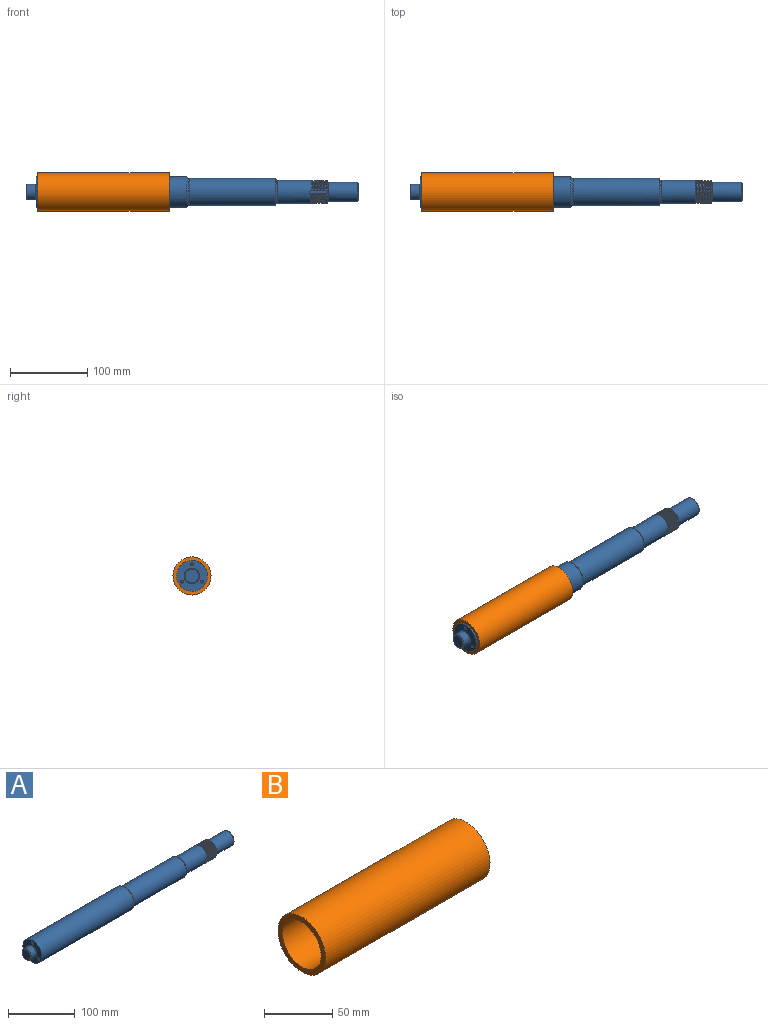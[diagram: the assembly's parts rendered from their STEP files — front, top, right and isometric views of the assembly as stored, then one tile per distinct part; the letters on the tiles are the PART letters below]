
ASSEMBLY  parts=2 mates=1
PART A: 82 faces, bbox 429x40x40 mm
  f0: cylinder r=15mm len=30mm, axis (-1,0,0), area 22.3mm2, adj f11,f28,f61,f63
  f1: cylinder r=15mm len=30mm, axis (-1,0,0), area 22.3mm2, adj f12,f29,f61,f63
  f2: cylinder r=15mm len=30mm, axis (-1,0,0), area 22.3mm2, adj f13,f30,f61,f63
  f3: cylinder r=15mm len=30mm, axis (-1,0,0), area 22.3mm2, adj f14,f31,f61,f63
  f4: cylinder r=15mm len=30mm, axis (-1,0,0), area 22.3mm2, adj f15,f32,f61,f63
  f5: cylinder r=15mm len=30mm, axis (-1,0,0), area 22.3mm2, adj f16,f33,f61,f63
  f6: cylinder r=15mm len=30mm, axis (-1,0,0), area 22.3mm2, adj f17,f34,f61,f63
  f7: cylinder r=15mm len=30mm, axis (-1,0,0), area 22.3mm2, adj f18,f35,f61,f63
  f8: cylinder r=15mm len=30mm, axis (-1,0,0), area 22.3mm2, adj f36,f55,f61,f63
  f9: cylinder r=15mm len=30mm, axis (-1,0,0), area 89.2mm2, adj f10,f48,f61,f63
  f10: bspline ~31.54x30mm, area 107.3mm2, adj f9,f19,f61,f63
  f11: bspline ~31.54x30mm, area 107.3mm2, adj f0,f20,f61,f63
  f12: bspline ~31.54x30mm, area 107.3mm2, adj f1,f21,f61,f63
  f13: bspline ~31.54x30mm, area 107.3mm2, adj f2,f22,f61,f63
  f14: bspline ~31.54x30mm, area 107.3mm2, adj f3,f23,f61,f63
  f15: bspline ~31.54x30mm, area 107.3mm2, adj f4,f24,f61,f63
  f16: bspline ~31.54x30mm, area 107.3mm2, adj f5,f25,f61,f63
  f17: bspline ~31.54x30mm, area 107.3mm2, adj f6,f26,f61,f63
  f18: bspline ~31.54x30mm, area 107.3mm2, adj f7,f27,f61,f63
  f19: cylinder r=13.92mm len=27.84mm, axis (1,0,0), area 41.2mm2, adj f10,f28,f61,f63
  f20: cylinder r=13.92mm len=27.84mm, axis (1,0,0), area 41.2mm2, adj f11,f29,f61,f63
  f21: cylinder r=13.92mm len=27.84mm, axis (1,0,0), area 41.2mm2, adj f12,f30,f61,f63
  f22: cylinder r=13.92mm len=27.84mm, axis (1,0,0), area 41.2mm2, adj f13,f31,f61,f63
  f23: cylinder r=13.92mm len=27.84mm, axis (1,0,0), area 41.2mm2, adj f14,f32,f61,f63
  f24: cylinder r=13.92mm len=27.84mm, axis (1,0,0), area 41.2mm2, adj f15,f33,f61,f63
  f25: cylinder r=13.92mm len=27.84mm, axis (1,0,0), area 41.2mm2, adj f16,f34,f61,f63
  f26: cylinder r=13.92mm len=27.84mm, axis (1,0,0), area 41.2mm2, adj f17,f35,f61,f63
  f27: cylinder r=13.92mm len=27.84mm, axis (1,0,0), area 41.2mm2, adj f18,f36,f61,f63
  f28: bspline ~31.54x30mm, area 107.3mm2, adj f0,f19,f61,f63
  f29: bspline ~31.54x30mm, area 107.3mm2, adj f1,f20,f61,f63
  f30: bspline ~31.54x30mm, area 107.3mm2, adj f2,f21,f61,f63
  f31: bspline ~31.54x30mm, area 107.3mm2, adj f3,f22,f61,f63
  f32: bspline ~31.54x30mm, area 107.3mm2, adj f4,f23,f61,f63
  f33: bspline ~31.54x30mm, area 107.3mm2, adj f5,f24,f61,f63
  f34: bspline ~31.54x30mm, area 107.3mm2, adj f6,f25,f61,f63
  f35: bspline ~31.54x30mm, area 107.3mm2, adj f7,f26,f61,f63
  f36: bspline ~31.54x30mm, area 107.3mm2, adj f8,f27,f61,f63
  f37: cylinder r=17.5mm len=111mm, axis (-1,0,0), area 12205.1mm2, adj f39,f40
  f38: plane 31x31mm, normal (1,0,0), area 94.2mm2, adj f39,f46
  f39: cone r=17.5mm half-angle=45deg, axis (-1,0,0), area 293.2mm2, adj f37,f38
  f40: plane 35x35mm, normal (-1,0,0), area 54.2mm2, adj f37,f41
  f41: cylinder r=17mm len=34mm, axis (-1,0,0), area 106.8mm2, adj f40,f44
  f42: cylinder r=20mm len=195mm, axis (-1,0,0), area 24504.4mm2, adj f43,f77
  f43: cone r=20mm half-angle=45deg, axis (-1,0,0), area 337.7mm2, adj f42,f44
  f44: plane 36x36mm, normal (1,0,0), area 110mm2, adj f41,f43
  f45: plane 30x30mm, normal (-1,0,0), area 46.3mm2, adj f46,f49
  f46: cylinder r=14.5mm len=29mm, axis (-1,0,0), area 91.1mm2, adj f38,f45
  f47: plane 28x27.81mm, normal (1,0,0), area 156.8mm2, adj f48,f51,f58,f59,f60
  f48: cone r=15mm half-angle=45deg, axis (-1,0,0), area 121.9mm2, adj f9,f47,f58,f59
  f49: cylinder r=15mm len=44.2mm, axis (-1,0,0), area 4069.8mm2, adj f45,f57,f62,f63
  f50: plane 25x25mm, normal (-1,0,0), area 38.5mm2, adj f51,f54
  f51: cylinder r=12mm len=24mm, axis (-1,0,0), area 75.4mm2, adj f47,f50
  f52: plane 23x23mm, normal (1,0,0), area 364.6mm2, adj f53,f65
  f53: cone r=12.5mm half-angle=45deg, axis (-1,0,0), area 106.6mm2, adj f52,f54
  f54: cylinder r=12.5mm len=37mm, axis (-1,0,0), area 2906mm2, adj f50,f53
  f55: bspline ~31.54x30mm, area 107.3mm2, adj f8,f56,f61,f62,f63
  f56: cylinder r=13.92mm len=27.84mm, axis (1,0,0), area 41.3mm2, adj f55,f57,f62,f63
  f57: bspline ~31.54x30mm, area 107.9mm2, adj f49,f56,f62,f63
  f58: cylinder r=2.5mm len=2.29mm, axis (0,-1,0), area 1.9mm2, adj f47,f48,f60,f63
  f59: cylinder r=2.5mm len=2.29mm, axis (0,-1,0), area 1.9mm2, adj f47,f48,f60,f61
  f60: plane 23.5x5mm, normal (0,-1,0), area 114.7mm2, adj f47,f58,f59,f61,f62,f63
  f61: plane 20.01x2.3mm, normal (0,0,1), area 34.7mm2, adj f0,f1,f2,f3,f4,f5,f6,f7
  f62: cylinder r=2.5mm len=5mm, axis (0,-1,0), area 17.5mm2, adj f49,f55,f56,f57,f60,f61,f63
  f63: plane 20.01x2.3mm, normal (0,0,-1), area 33.4mm2, adj f0,f1,f2,f3,f4,f5,f6,f7
  f64: cylinder r=3.4mm len=30.13mm, axis (1,0,0), area 643.6mm2, adj f65,f78
  f65: cone r=4.03mm half-angle=45deg, axis (1,0,0), area 20.6mm2, adj f52,f64
  f66: plane 18x18mm, normal (-1,0,0), area 254.5mm2, adj f67
  f67: cone r=9mm half-angle=45deg, axis (1,0,0), area 84.4mm2, adj f66,f68
  f68: cylinder r=10mm len=20mm, axis (-1,0,0), area 691.2mm2, adj f67,f72
  f69: cylinder r=1.65mm len=11.73mm, axis (-1,0,0), area 121.6mm2, adj f73,f81
  f70: cylinder r=1.65mm len=11.73mm, axis (-1,0,0), area 121.6mm2, adj f74,f80
  f71: cylinder r=1.65mm len=11.73mm, axis (-1,0,0), area 121.6mm2, adj f75,f79
  f72: plane 20x20mm, normal (1,0,0), area 30.6mm2, adj f68,f76
  f73: cone r=2.02mm half-angle=45deg, axis (-1,0,0), area 6.1mm2, adj f69,f77
  f74: cone r=2.02mm half-angle=45deg, axis (-1,0,0), area 6.1mm2, adj f70,f77
  f75: cone r=2.02mm half-angle=45deg, axis (-1,0,0), area 6.1mm2, adj f71,f77
  f76: cylinder r=9.5mm len=19mm, axis (1,0,0), area 59.7mm2, adj f72,f77
  f77: plane 40x40mm, normal (-1,0,0), area 934.5mm2, adj f42,f73,f74,f75,f76
  f78: cone r=0mm half-angle=59deg, axis (1,0,0), area 42.4mm2, adj f64
  f79: cone r=0mm half-angle=59deg, axis (-1,0,0), area 10mm2, adj f71
  f80: cone r=0mm half-angle=59deg, axis (-1,0,0), area 10mm2, adj f70
  f81: cone r=0mm half-angle=59deg, axis (-1,0,0), area 10mm2, adj f69
PART B: 4 faces, bbox 170x49.2x49.2 mm
  f0: cylinder r=20mm len=170mm, axis (-1,0,0), area 21362.8mm2, adj f2,f3
  f1: cylinder r=24.6mm len=170mm, axis (-1,0,0), area 26276.3mm2, adj f2,f3
  f2: plane 49.2x49.2mm, normal (1,0,0), area 644.5mm2, adj f0,f1
  f3: plane 49.2x49.2mm, normal (-1,0,0), area 644.5mm2, adj f0,f1
PLACE A t=(-45.42,66.24,-47.06)mm
PLACE B t=(-30.42,66.24,-47.06)mm
MATE fastened B.f0 <-> A.f0  axis (-1,0,0) through (-30.42,66.24,-47.06)mm
